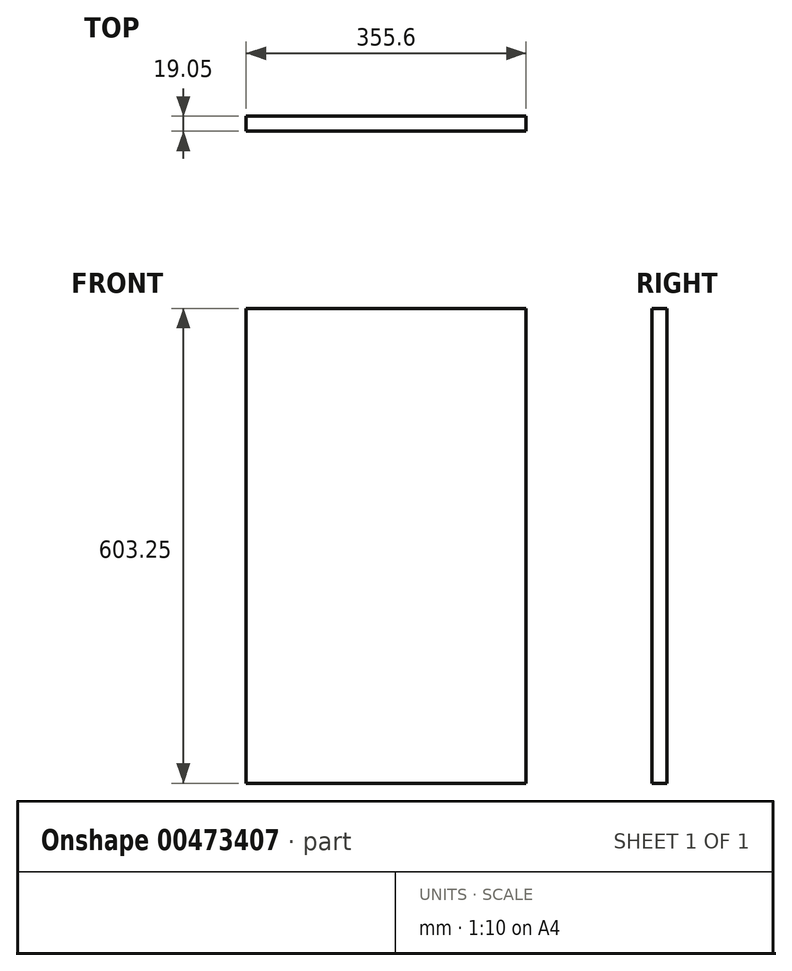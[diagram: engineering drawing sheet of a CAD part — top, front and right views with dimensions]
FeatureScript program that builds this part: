
annotation { "Feature Type Name" : "Feature", "Feature Type Description" : "" }
export const myFeature = defineFeature(function(context is Context, id is Id, definition is map)
    precondition{}
    {
        {
            var Q0;
            Q0=qCreatedBy(makeId("Front.planeOp"),FACE);
            var sketch = newSketch(context, id + "F0", { "sketchPlane" : qUnion([Q0])});
            skLineSegment(sketch, "E0.bottom", {"start": v(0, 0) * mm, "end": v(355.6, 0) * mm});
            skLineSegment(sketch, "E0.top", {"start": v(0, 603.25) * mm, "end": v(355.6, 603.25) * mm});
            skLineSegment(sketch, "E0.left", {"start": v(0, 0) * mm, "end": v(0, 603.25) * mm});
            skLineSegment(sketch, "E0.right", {"start": v(355.6, 0) * mm, "end": v(355.6, 603.25) * mm});
            skSolve(sketch);
        }
        {
            var Q0;
            Q0=makeQuery(id+"F0.imprint","IMPRINT",FACE,{"disambiguationData":[TD([[makeQuery(id+"F0.imprint","IMPRINT",EDGE,{"derivedFrom":sQuery(id+"F0.wireOp",EDGE,"E0.bottom")}),1.0]])]});
            extrude(context, id + "F1", {"entities" : qUnion([Q0]), "depth" : 19.05 * mm});
        }
    });
